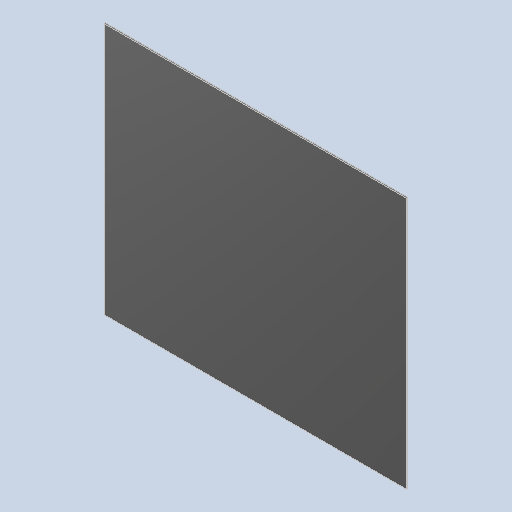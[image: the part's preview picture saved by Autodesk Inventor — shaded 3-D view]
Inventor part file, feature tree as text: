
AUTODESK INVENTOR PART (.ipt)
format: ipt  version: 2024 (Build 280153000, 153)  size: 201,728 bytes
history: native  units: mm
features: extrude x1, sketch x1
ambient origin geometry x8: Origin, YZ Plane, XZ Plane, XY Plane, X Axis, Y Axis, Z Axis, Center Point
bodies: Solid1 (feature_tree)
feature tree (2):
  extrude  "Extrusion1"  Depth=250.0mm
  sketch  "Sketch1"  dims[d0=300.0mm d1=250.0mm d2=1.5mm d3=0.0mm]
